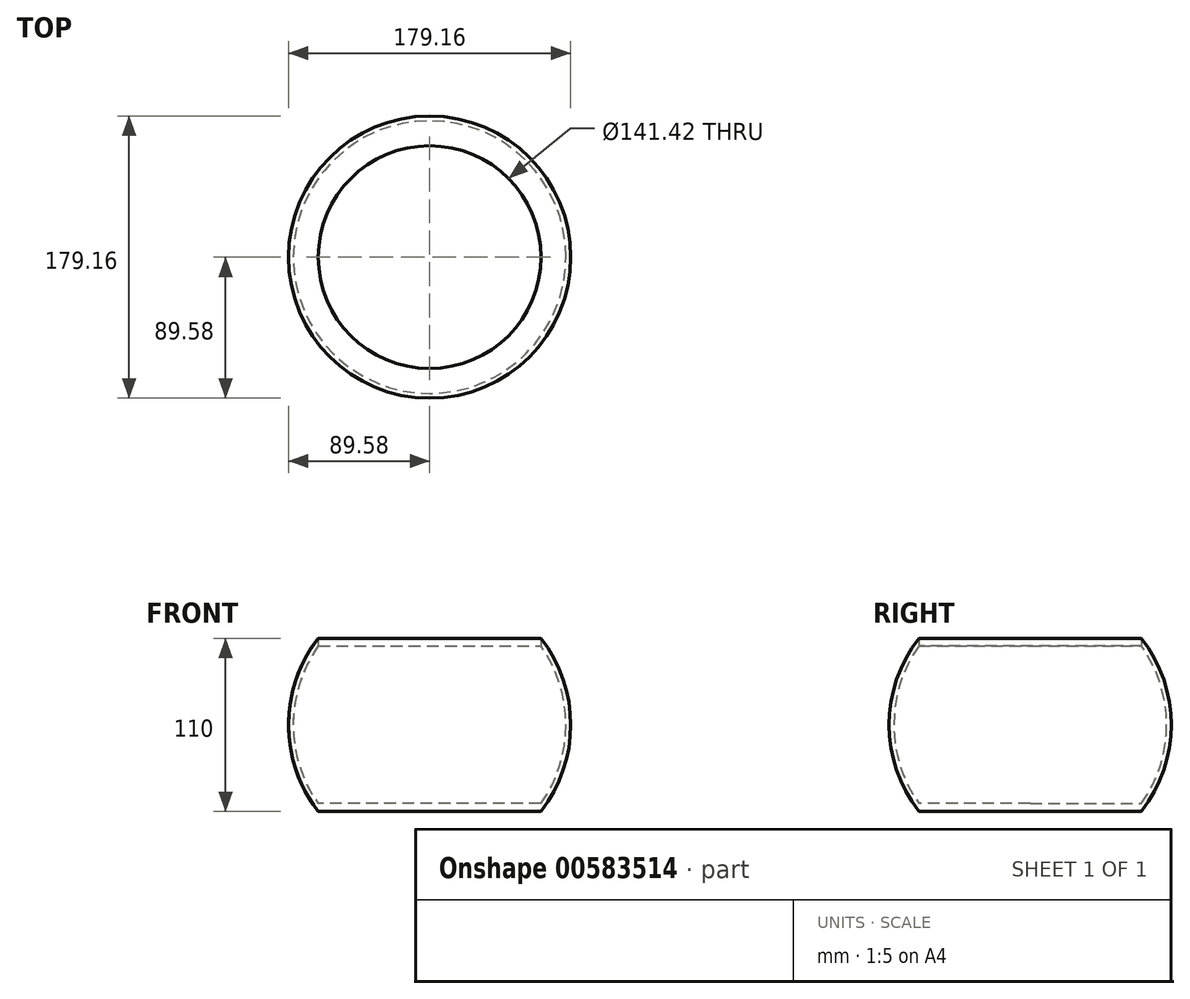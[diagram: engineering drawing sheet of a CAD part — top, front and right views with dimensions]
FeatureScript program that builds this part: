
annotation { "Feature Type Name" : "Feature", "Feature Type Description" : "" }
export const myFeature = defineFeature(function(context is Context, id is Id, definition is map)
    precondition{}
    {
        {
            var Q0;
            Q0=qCreatedBy(makeId("Top.planeOp"),FACE);
            var sketch = newSketch(context, id + "F0", { "sketchPlane" : qUnion([Q0])});
            skLineSegment(sketch, "E0.bottom", {"start": v(-50, 50) * mm, "end": v(50, 50) * mm});
            skLineSegment(sketch, "E0.top", {"start": v(-50, -50) * mm, "end": v(50, -50) * mm});
            skLineSegment(sketch, "E0.left", {"start": v(-50, 50) * mm, "end": v(-50, -50) * mm});
            skLineSegment(sketch, "E0.right", {"start": v(50, 50) * mm, "end": v(50, -50) * mm});
            skSolve(sketch);
        }
        {
            var Q0;
            Q0 = qSketchRegion(id + "F0", true);
            extrude(context, id + "F1", {"entities" : qUnion([Q0]), "depth" : 5 * mm, "offsetDistance" : 25 * mm});
        }
        {
            var Q0;
            Q0=makeQuery(id+"F1.opExtrude","SWEPT_FACE",FACE,{"disambiguationData":[OSD([sQuery(id+"F0.wireOp",EDGE,"E0.left")])]});
            cPlane(context, id + "F2", {"entities" : qUnion([Q0]), "cplaneType" : CPlaneType.OFFSET, "offset" : 0 * mm, "width" : 150 * mm, "height" : 150 * mm});
        }
        {
            var Q0;
            Q0=qCreatedBy(id+"FmG7JSVAYBJ5sxI_1.planeOp",FACE);
            var sketch = newSketch(context, id + "F3", { "sketchPlane" : qUnion([Q0])});
            skLineSegment(sketch, "E1.bottom", {"start": v(50, 50) * mm, "end": v(-50, 50) * mm});
            skLineSegment(sketch, "E1.top", {"start": v(50, -50) * mm, "end": v(-50, -50) * mm});
            skLineSegment(sketch, "E1.left", {"start": v(50, 50) * mm, "end": v(50, -50) * mm});
            skLineSegment(sketch, "E1.right", {"start": v(-50, 50) * mm, "end": v(-50, -50) * mm});
            skSolve(sketch);
        }
        {
            var Q0;
            Q0=qCreatedBy(id+"F2.planeOp",FACE);
            var sketch = newSketch(context, id + "F4", { "sketchPlane" : qUnion([Q0])});
            skArc(sketch, "E2", {"start": v(50, 0) * mm, "mid": v(74.33, 55) * mm, "end": v(50, 110) * mm});
            skArc(sketch, "E3", {"start": v(50, 5) * mm, "mid": v(70.71, 55) * mm, "end": v(50, 105) * mm});
            skLineSegment(sketch, "E4", {"start": v(50, 110) * mm, "end": v(50, 105) * mm});
            skLineSegment(sketch, "E5", {"start": v(50, 5) * mm, "end": v(50, 0) * mm});
            skSolve(sketch);
        }
        {
            var Q0;
            Q0=makeQuery(id+"F1.opExtrude","SWEPT_FACE",FACE,{"disambiguationData":[OSD([sQuery(id+"F0.wireOp",EDGE,"E0.left")])]});
            cPlane(context, id + "F5", {"entities" : qUnion([Q0]), "cplaneType" : CPlaneType.OFFSET, "offset" : 50 * mm, "oppositeDirection" : true, "width" : 150 * mm, "height" : 150 * mm});
        }
        {
            var Q0;
            Q0=qCreatedBy(id+"F5.planeOp",FACE);
            var sketch = newSketch(context, id + "F6", { "sketchPlane" : qUnion([Q0])});
            skLineSegment(sketch, "E6", {"start": v(0, 0) * mm, "end": v(0, 112.49) * mm});
            skSolve(sketch);
        }
        {
            var Q0;
            Q0 = qSketchRegion(id + "F4", true);
            var Q1;
            Q1=sQuery(id+"F6.wireOp",EDGE,"E6");
            revolve(context, id + "F7", {"entities" : qUnion([Q0]), "axis" : qUnion([Q1]), "revolveType" : RevolveType.FULL});
        }
        {
            var Q0;
            Q0=qCreatedBy(makeId("Top.planeOp"),FACE);
            var sketch = newSketch(context, id + "F8", { "sketchPlane" : qUnion([Q0])});
            skCircle(sketch, "E7", {"center": v(0, 0) * mm, "radius": 70.71 * mm});
            skSolve(sketch);
        }
        {
            var Q0;
            Q0 = qSketchRegion(id + "F8", true);
            extrude(context, id + "F9", {"entities" : qUnion([Q0]), "operationType" : NewBodyOperationType.ADD, "depth" : 5 * mm, "offsetDistance" : 25 * mm});
        }
    });
